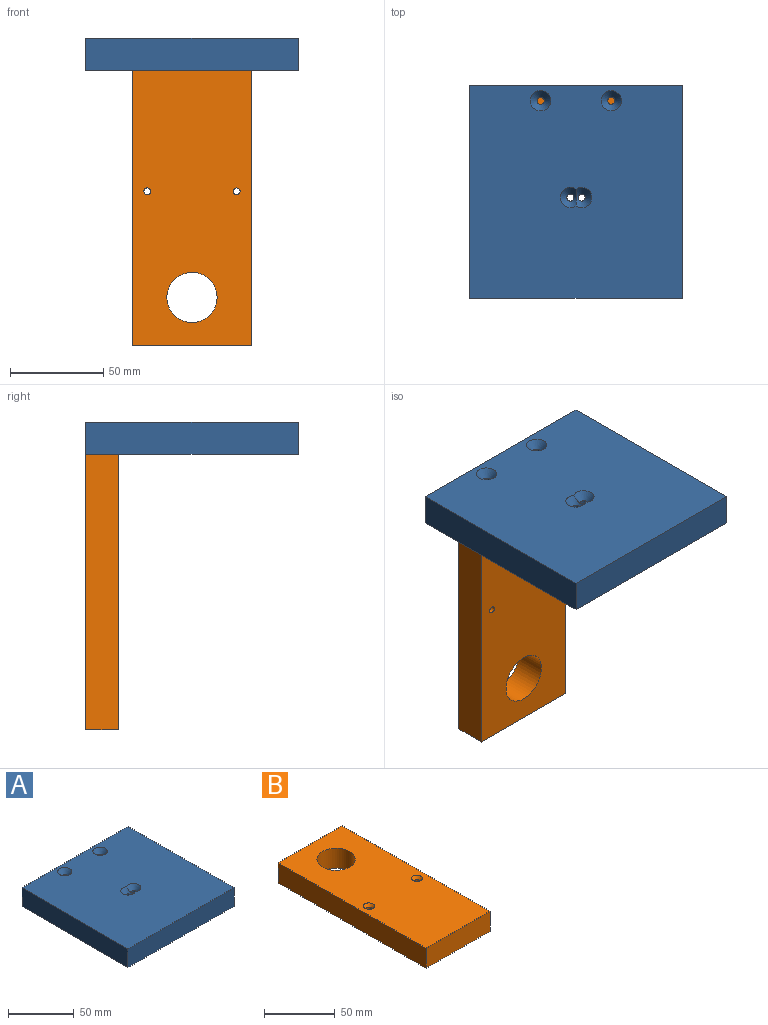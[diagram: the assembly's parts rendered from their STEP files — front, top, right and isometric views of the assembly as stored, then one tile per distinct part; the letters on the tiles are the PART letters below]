
ASSEMBLY  parts=2 mates=1
PART A: 14 faces, bbox 114x114x17.3 mm
  f0: plane 114x114mm, normal (0,0,1), area 12651.4mm2, adj f1,f2,f3,f4,f5,f8,f10,f13
  f1: cone r=1.91mm half-angle=41deg, axis (0,0,1), area 101.8mm2, adj f0,f11,f13
  f2: plane 114x17.3mm, normal (1,0,0), area 1972.2mm2, adj f0,f3,f5,f6
  f3: plane 114x17.3mm, normal (0,1,0), area 1972.2mm2, adj f0,f2,f4,f6
  f4: plane 114x17.3mm, normal (-1,0,0), area 1972.2mm2, adj f0,f3,f5,f6
  f5: plane 114x17.3mm, normal (0,-1,0), area 1972.2mm2, adj f0,f2,f4,f6
  f6: plane 114x114mm, normal (0,0,-1), area 12950.4mm2, adj f2,f3,f4,f5,f7,f9,f11,f12
  f7: cylinder r=1.91mm len=13.19mm, axis (0,0,1), area 157.9mm2, adj f6,f8
  f8: cone r=1.91mm half-angle=41deg, axis (0,0,1), area 126.1mm2, adj f0,f7
  f9: cylinder r=1.91mm len=13.19mm, axis (0,0,1), area 157.9mm2, adj f6,f10
  f10: cone r=1.91mm half-angle=41deg, axis (0,0,1), area 126.1mm2, adj f0,f9
  f11: cylinder r=1.91mm len=13.19mm, axis (0,0,1), area 157.9mm2, adj f1,f6
  f12: cylinder r=1.91mm len=13.19mm, axis (0,0,1), area 157.9mm2, adj f6,f13
  f13: cone r=1.91mm half-angle=41deg, axis (0,0,1), area 101.8mm2, adj f0,f1,f12
PART B: 11 faces, bbox 64x148x17.3 mm
  f0: plane 148x17.3mm, normal (1,0,0), area 2560.4mm2, adj f1,f3,f4,f5
  f1: plane 64x17.3mm, normal (0,1,0), area 1107.2mm2, adj f0,f2,f4,f5
  f2: plane 148x17.3mm, normal (-1,0,0), area 2560.4mm2, adj f1,f3,f4,f5
  f3: plane 64x17.3mm, normal (0,-1,0), area 1107.2mm2, adj f0,f2,f4,f5
  f4: plane 148x64mm, normal (0,0,1), area 8804.5mm2, adj f0,f1,f2,f3,f6,f8,f10
  f5: plane 148x64mm, normal (0,0,-1), area 8879mm2, adj f0,f1,f2,f3,f6,f7,f9
  f6: cylinder r=13.49mm len=26.99mm, axis (0,0,1), area 1466.8mm2, adj f4,f5
  f7: cylinder r=1.83mm len=14.92mm, axis (0,0,1), area 171.4mm2, adj f5,f8
  f8: cone r=1.83mm half-angle=41deg, axis (0,0,1), area 56.8mm2, adj f4,f7
  f9: cylinder r=1.83mm len=14.92mm, axis (0,0,1), area 171.4mm2, adj f5,f10
  f10: cone r=1.83mm half-angle=41deg, axis (0,0,1), area 56.8mm2, adj f4,f9
PLACE A t=(-1.03,6.86,47.38)mm
PLACE B rot(axis=(-1,0,0),90deg) t=(-1.03,46.56,-26.62)mm
MATE fastened B.f3 <-> A.f6  axis (0,0,1) through (-1.03,63.86,47.38)mm
